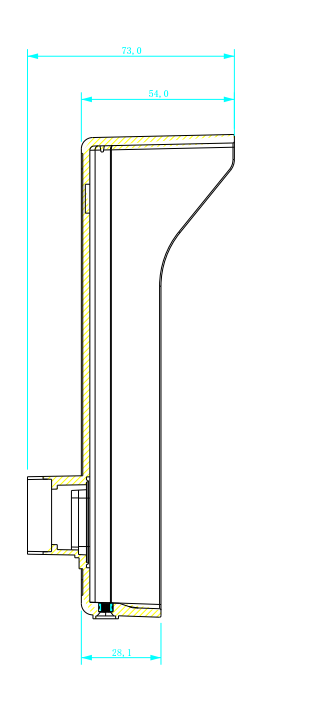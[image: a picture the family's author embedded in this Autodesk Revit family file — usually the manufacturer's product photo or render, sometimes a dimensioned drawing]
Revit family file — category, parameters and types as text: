
# Revit family: SH-45T
name_source: partatom
category: Устройства связи
units: mm (PartAtom-declared; Revit-internal decimal feet)

## family parameters
Всегда вертикально = Нет
На основе рабочей плоскости = Да
Общий = Да
При загрузке вырезать с полостями = Нет
Размер круглого соединителя = Использовать диаметр
Сохранять ориентацию аннотаций = Нет
Тип детали = Нормальный
Точка принадлежности помещению = Нет

## types (1)
- SH-45T
    ADSK_URL документации изделия = -
    ADSK_URL страницы изделия = https://www.bas-ip.ru
    ADSK_Версия Revit = Revit 2020
    ADSK_Единица измерения = шт
    ADSK_Завод-изготовитель = BAS-IP
    ADSK_Классификация нагрузок = Кнопка выхода бесконтактная
    ADSK_Количество фаз = 1
    ADSK_Коэффициент мощности = 0.9
    ADSK_Марка = SH-45T
    ADSK_Наименование = Кнопка выхода бесконтактная SH-45T
    ADSK_Наименование краткое = SH-45T
    ADSK_Напряжение = 12 В
    ADSK_Номинальная мощность = 1 Вт
    ADSK_Полная мощность = 1 В·А
    ADSK_Размер_Длина = 114 мм
    ADSK_Размер_Толщина = 20 мм
    ADSK_Размер_Ширина = 70 мм
    BIM library = https://bimlib.ru
    URL = https://www.bas-ip.ru
    Группа модели = Кнопка выхода бесконтактная SH-45T
    Дополнительно = • Возможность изменения (переключения) цвета подсветки
• Триггерный режим
• Пластина из нержавеющей стали AISI 316
    Допустимая влажность = 10% – 94%
    Изготовитель = BAS-IP
    Изображение типоразмера = <Нет>
    Материал корпуса = Материал серый
    Межосевое расстояние для винтов крепления = 83 мм
    Метод нанесения покрытия кнопки = Анодирование
    Напряжение питания = +12В (+1%, - 15%)
    Описание = Кнопка выхода бесконтактная SH-45T - Бесконтактная кнопка выхода с ресурсом работы более чем 100 миллионов нажатий. Срабатывание на расстоянии от 15 до 20 см. ВАЖНО! Категорически запрещается для питания кнопки SH-45TR использовать блок питания, который используется для питания замка! Необходимо использовать отдельный блок питания, к которому замки и другое оборудование, с высоким потреблением, не подключены!
    Отметка по умолчанию = 0 мм
    Размеры = 70×114×19,5 мм
    Расстояние (радиус) от центра до отверстия под винт = 41,5 мм
    Ресурс работы = Более 100 миллионов нажатий
    Степень защиты = IP68
    Температурный режим = -27 – +60 °C
    Тип кнопки = Бесконтактная
    Цвет = Черный, серебро
